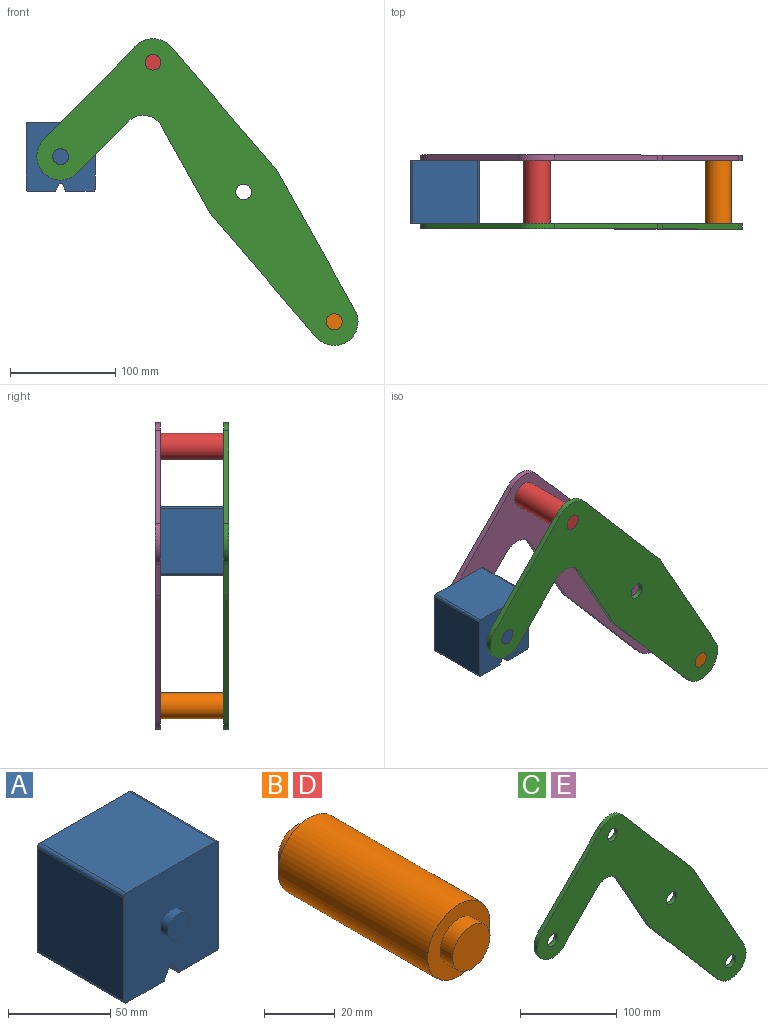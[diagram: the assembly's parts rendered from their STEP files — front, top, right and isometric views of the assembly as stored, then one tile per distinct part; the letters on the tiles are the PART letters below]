
ASSEMBLY  parts=5 mates=3
PART A: 18 faces, bbox 65.6x70x65.6 mm
  f0: plane 60x6.42mm, normal (-0.89,0,-0.45), area 430.8mm2, adj f4,f6,f10,f13
  f1: plane 60x6.42mm, normal (0.89,0,-0.45), area 430.8mm2, adj f2,f4,f10,f13
  f2: plane 60x25.78mm, normal (0,0,-1), area 1547mm2, adj f1,f4,f10,f14
  f3: plane 61.57x60mm, normal (-1,0,0), area 3694.1mm2, adj f4,f10,f14,f15
  f4: plane 65.57x65.57mm, normal (0,-1,0), area 4072.6mm2, adj f0,f1,f2,f3,f5,f6,f7,f9
  f5: plane 61.57x60mm, normal (0,0,1), area 3694.1mm2, adj f4,f10,f15,f16
  f6: plane 60x25.78mm, normal (0,0,-1), area 1547mm2, adj f0,f4,f10,f17
  f7: plane 61.57x60mm, normal (1,0,0), area 3694.1mm2, adj f4,f10,f16,f17
  f8: plane 15x15mm, normal (0,-1,0), area 176.7mm2, adj f9
  f9: cylinder r=7.5mm len=15mm, axis (0,1,0), area 235.6mm2, adj f4,f8
  f10: plane 65.57x65.57mm, normal (0,1,0), area 4072.6mm2, adj f0,f1,f2,f3,f5,f6,f7,f12
  f11: plane 15x15mm, normal (0,1,0), area 176.7mm2, adj f12
  f12: cylinder r=7.5mm len=15mm, axis (0,-1,0), area 235.6mm2, adj f10,f11
  f13: cylinder r=2mm len=60mm, axis (0,-1,0), area 265.7mm2, adj f0,f1,f4,f10
  f14: cylinder r=2mm len=60mm, axis (0,-1,0), area 188.5mm2, adj f2,f3,f4,f10
  f15: cylinder r=2mm len=60mm, axis (0,1,0), area 188.5mm2, adj f3,f4,f5,f10
  f16: cylinder r=2mm len=60mm, axis (0,-1,0), area 188.5mm2, adj f4,f5,f7,f10
  f17: cylinder r=2mm len=60mm, axis (0,1,0), area 188.5mm2, adj f4,f6,f7,f10
PART B: 7 faces, bbox 25x70x25 mm
  f0: cylinder r=12.5mm len=60mm, axis (0,-1,0), area 4712.4mm2, adj f1,f4
  f1: plane 25x25mm, normal (0,-1,0), area 314.2mm2, adj f0,f2
  f2: cylinder r=7.5mm len=15mm, axis (0,1,0), area 235.6mm2, adj f1,f3
  f3: plane 15x15mm, normal (0,-1,0), area 176.7mm2, adj f2
  f4: plane 25x25mm, normal (0,1,0), area 314.2mm2, adj f0,f5
  f5: cylinder r=7.5mm len=15mm, axis (0,-1,0), area 235.6mm2, adj f4,f6
  f6: plane 15x15mm, normal (0,1,0), area 176.7mm2, adj f5
PART C: 18 faces, bbox 304.4x5x290.9 mm
  f0: plane 80.77x45.15mm, normal (-0.87,0,-0.49), area 462.7mm2, adj f1,f14,f16,f17
  f1: cylinder r=37.5mm len=6.15mm, axis (0,1,0), area 37.6mm2, adj f0,f2,f16,f17
  f2: plane 113.18x97.29mm, normal (-0.76,0,-0.65), area 746.2mm2, adj f1,f3,f16,f17
  f3: cylinder r=22.5mm len=39.56mm, axis (0,1,0), area 330.9mm2, adj f2,f4,f16,f17
  f4: plane 130.27x72.83mm, normal (0.87,0,0.49), area 746.2mm2, adj f3,f5,f16,f17
  f5: cylinder r=37.5mm len=6.15mm, axis (0,1,0), area 37.6mm2, adj f4,f6,f16,f17
  f6: plane 113.18x97.29mm, normal (0.76,0,0.65), area 746.2mm2, adj f5,f7,f16,f17
  f7: cylinder r=22.5mm len=34.12mm, axis (0,1,0), area 193.7mm2, adj f6,f8,f16,f17
  f8: plane 88.06x86.58mm, normal (-0.71,0,0.7), area 617.5mm2, adj f7,f9,f16,f17
  f9: cylinder r=22.5mm len=38.55mm, axis (0,1,0), area 353.5mm2, adj f8,f10,f16,f17
  f10: plane 48.72x47.86mm, normal (0.71,0,-0.7), area 341.4mm2, adj f9,f14,f16,f17
  f11: cylinder r=7.5mm len=15mm, axis (0,1,0), area 235.6mm2, adj f16,f17
  f12: cylinder r=7.5mm len=15mm, axis (0,1,0), area 235.6mm2, adj f16,f17
  f13: cylinder r=7.5mm len=15mm, axis (0,1,0), area 235.6mm2, adj f16,f17
  f14: cylinder r=20mm len=31.72mm, axis (0,1,0), area 185.5mm2, adj f0,f10,f16,f17
  f15: cylinder r=7.5mm len=15mm, axis (0,1,0), area 235.6mm2, adj f16,f17
  f16: plane 304.44x290.91mm, normal (0,-1,0), area 24552.3mm2, adj f0,f1,f2,f3,f4,f5,f6,f7
  f17: plane 304.44x290.91mm, normal (0,1,0), area 24552.3mm2, adj f0,f1,f2,f3,f4,f5,f6,f7
PART D: same geometry as B
PART E: same geometry as C
PLACE A t=(0,-30,-0.34)mm
PLACE B t=(171.84,-30,-245.91)mm
PLACE C t=(0,-30,0)mm fixed
PLACE D t=(0,-30,0)mm
PLACE E t=(0,35,0)mm
MATE fastened E.f7 <-> D.f0  axis (0,-1,0) through (-85.92,30,122.95)mm
MATE revolute A.f4 <-> C.f9  axis (0,-1,0) through (-173.52,-30,33.78)mm
MATE fastened B.f0 <-> C.f3  axis (0,-1,0) through (85.92,-30,-122.95)mm
